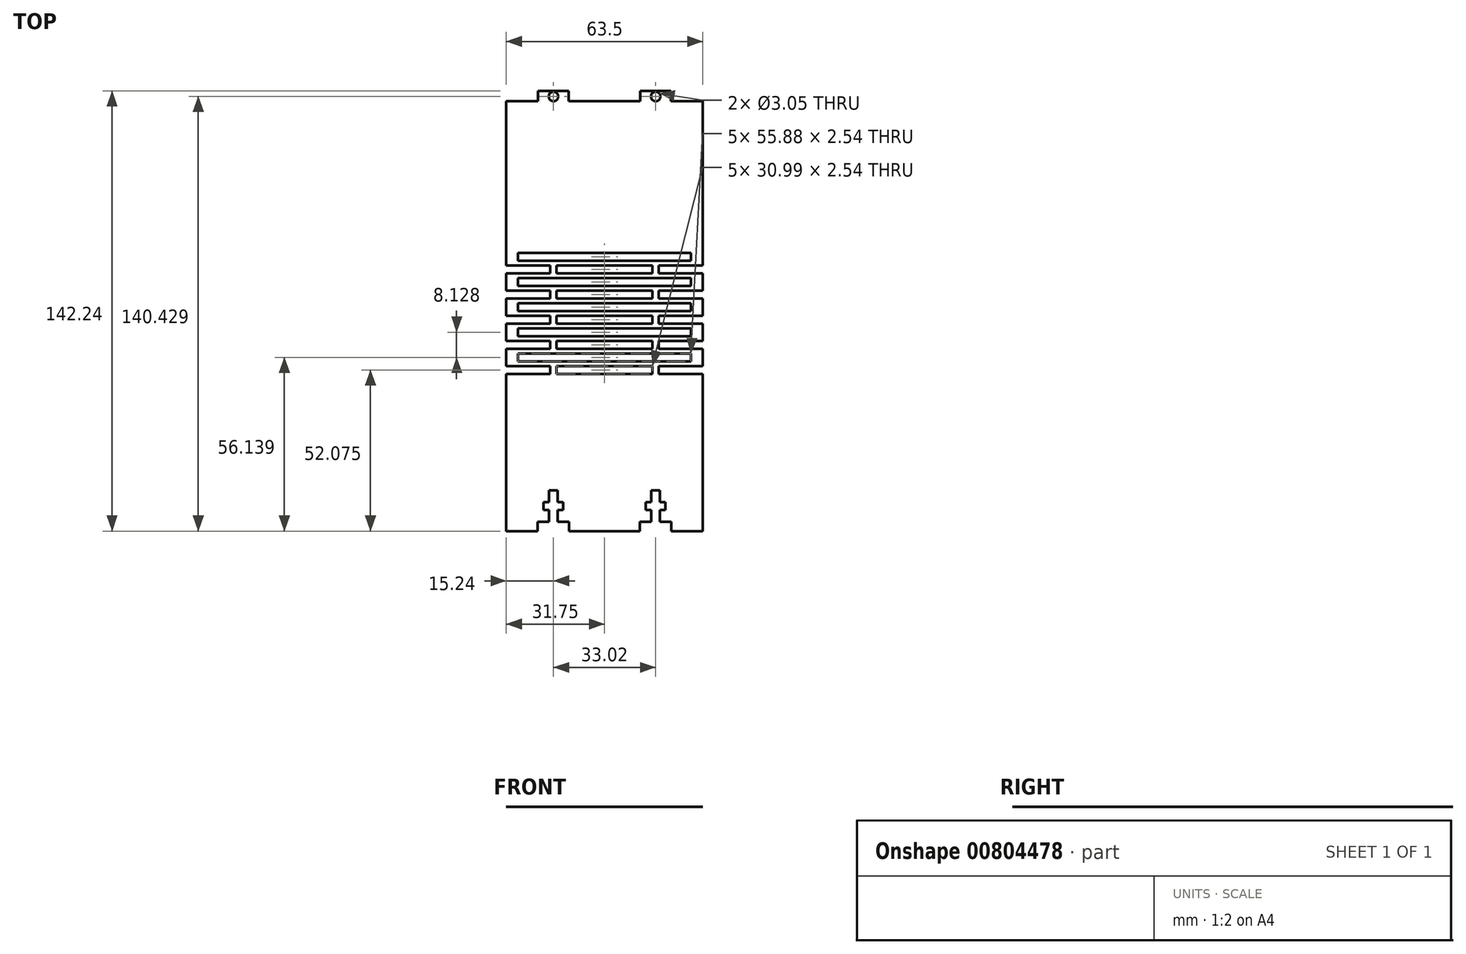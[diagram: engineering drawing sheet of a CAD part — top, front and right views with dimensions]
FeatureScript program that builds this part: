
annotation { "Feature Type Name" : "Feature", "Feature Type Description" : "" }
export const myFeature = defineFeature(function(context is Context, id is Id, definition is map)
    precondition{}
    {
        {
            var Q0;
            Q0=qCreatedBy(makeId("Top.planeOp"),FACE);
            var sketch = newSketch(context, id + "F0", { "sketchPlane" : qUnion([Q0])});
            skLineSegment(sketch, "E0.bottom", {"start": v(31.75, -64.45) * mm, "end": v(-31.75, -64.45) * mm});
            skLineSegment(sketch, "E1", {"start": v(-21.59, -64.45) * mm, "end": v(-21.59, -61.4) * mm});
            skLineSegment(sketch, "E2", {"start": v(-21.59, -61.4) * mm, "end": v(-17.9, -61.4) * mm});
            skLineSegment(sketch, "E3", {"start": v(-17.9, -61.4) * mm, "end": v(-17.9, -57.59) * mm});
            skLineSegment(sketch, "E4", {"start": v(-17.9, -57.59) * mm, "end": v(-19.69, -57.59) * mm});
            skLineSegment(sketch, "E5", {"start": v(-19.69, -57.59) * mm, "end": v(-19.69, -55.05) * mm});
            skLineSegment(sketch, "E6", {"start": v(-19.69, -55.05) * mm, "end": v(-17.9, -55.05) * mm});
            skLineSegment(sketch, "E7", {"start": v(-17.9, -55.05) * mm, "end": v(-17.9, -51.24) * mm});
            skLineSegment(sketch, "E8", {"start": v(-17.9, -51.24) * mm, "end": v(-15.11, -51.24) * mm});
            skLineSegment(sketch, "E9", {"start": v(-15.11, -51.24) * mm, "end": v(-15.11, -55.05) * mm});
            skLineSegment(sketch, "E10", {"start": v(-15.11, -55.05) * mm, "end": v(-13.33, -55.05) * mm});
            skLineSegment(sketch, "E11", {"start": v(-13.33, -55.05) * mm, "end": v(-13.33, -57.59) * mm});
            skLineSegment(sketch, "E12", {"start": v(-13.33, -57.59) * mm, "end": v(-15.11, -57.59) * mm});
            skLineSegment(sketch, "E13", {"start": v(-15.11, -57.59) * mm, "end": v(-15.11, -61.4) * mm});
            skLineSegment(sketch, "E14", {"start": v(-15.11, -61.4) * mm, "end": v(-11.43, -61.4) * mm});
            skLineSegment(sketch, "E15", {"start": v(-11.43, -61.4) * mm, "end": v(-11.43, -64.45) * mm});
            skLineSegment(sketch, "E16", {"start": v(-17.9, -55.05) * mm, "end": v(-15.11, -55.05) * mm, "construction": true});
            skLineSegment(sketch, "E17", {"start": v(-17.9, -57.59) * mm, "end": v(-15.11, -57.59) * mm, "construction": true});
            skLineSegment(sketch, "E18", {"start": v(-17.9, -61.4) * mm, "end": v(-15.11, -61.4) * mm, "construction": true});
            skLineSegment(sketch, "E19", {"start": v(-17.9, -55.05) * mm, "end": v(-17.9, -57.59) * mm, "construction": true});
            skLineSegment(sketch, "E20", {"start": v(-15.11, -55.05) * mm, "end": v(-15.11, -57.59) * mm, "construction": true});
            skLineSegment(sketch, "E21", {"start": v(-21.46, 74.5) * mm, "end": v(-21.46, 77.8) * mm});
            skLineSegment(sketch, "E22", {"start": v(-21.46, 77.8) * mm, "end": v(-11.56, 77.8) * mm});
            skLineSegment(sketch, "E23", {"start": v(-11.56, 77.8) * mm, "end": v(-11.56, 74.5) * mm});
            skCircle(sketch, "E24", {"center": v(-16.5, 75.98) * mm, "radius": 1.52 * mm});
            skPoint(sketch, "E25", {"position": v(-16.5, 77.8) * mm});
            skLineSegment(sketch, "E26", {"start": v(-21.59, -64.45) * mm, "end": v(-11.43, -64.45) * mm, "construction": true});
            skPoint(sketch, "E27", {"position": v(-16.51, -64.45) * mm});
            skLineSegment(sketch, "E28", {"start": v(-16.51, -64.45) * mm, "end": v(-16.51, 77.8) * mm, "construction": true});
            skLineSegment(sketch, "E29.MirrorCS", {"start": v(17.9, -57.59) * mm, "end": v(15.11, -57.59) * mm, "construction": true});
            skLineSegment(sketch, "E30.MirrorCS", {"start": v(15.11, -55.05) * mm, "end": v(15.11, -57.59) * mm, "construction": true});
            skLineSegment(sketch, "E31.MirrorCS", {"start": v(17.9, -55.05) * mm, "end": v(15.11, -55.05) * mm, "construction": true});
            skLineSegment(sketch, "E32.MirrorCS", {"start": v(17.9, -55.05) * mm, "end": v(17.9, -57.59) * mm, "construction": true});
            skLineSegment(sketch, "E33.MirrorCS", {"start": v(17.9, -57.59) * mm, "end": v(19.69, -57.59) * mm});
            skLineSegment(sketch, "E34.MirrorCS", {"start": v(17.9, -61.4) * mm, "end": v(15.11, -61.4) * mm, "construction": true});
            skLineSegment(sketch, "E35.MirrorCS", {"start": v(15.11, -55.05) * mm, "end": v(13.33, -55.05) * mm});
            skLineSegment(sketch, "E36.MirrorCS", {"start": v(17.9, -51.24) * mm, "end": v(15.11, -51.24) * mm});
            skLineSegment(sketch, "E37.MirrorCS", {"start": v(11.43, -61.4) * mm, "end": v(11.43, -64.45) * mm});
            skLineSegment(sketch, "E38.MirrorCS", {"start": v(19.69, -55.05) * mm, "end": v(17.9, -55.05) * mm});
            skLineSegment(sketch, "E39.MirrorCS", {"start": v(19.69, -57.59) * mm, "end": v(19.69, -55.05) * mm});
            skLineSegment(sketch, "E40.MirrorCS", {"start": v(13.33, -55.05) * mm, "end": v(13.33, -57.59) * mm});
            skLineSegment(sketch, "E41.MirrorCS", {"start": v(13.33, -57.59) * mm, "end": v(15.11, -57.59) * mm});
            skLineSegment(sketch, "E42.MirrorCS", {"start": v(21.59, -64.45) * mm, "end": v(21.59, -61.4) * mm});
            skLineSegment(sketch, "E43.MirrorCS", {"start": v(17.9, -55.05) * mm, "end": v(17.9, -51.24) * mm});
            skLineSegment(sketch, "E44.MirrorCS", {"start": v(21.59, -64.45) * mm, "end": v(11.43, -64.45) * mm, "construction": true});
            skLineSegment(sketch, "E45.MirrorCS", {"start": v(15.11, -51.24) * mm, "end": v(15.11, -55.05) * mm});
            skLineSegment(sketch, "E46.MirrorCS", {"start": v(15.11, -57.59) * mm, "end": v(15.11, -61.4) * mm});
            skLineSegment(sketch, "E47.MirrorCS", {"start": v(17.9, -61.4) * mm, "end": v(17.9, -57.59) * mm});
            skLineSegment(sketch, "E48.MirrorCS", {"start": v(-31.75, -64.45) * mm, "end": v(31.75, -64.45) * mm});
            skLineSegment(sketch, "E49.MirrorCS", {"start": v(21.59, -61.4) * mm, "end": v(17.9, -61.4) * mm});
            skPoint(sketch, "E50.MirrorP", {"position": v(16.51, -64.45) * mm});
            skLineSegment(sketch, "E51.MirrorCS", {"start": v(16.51, -64.45) * mm, "end": v(16.51, 77.8) * mm, "construction": true});
            skLineSegment(sketch, "E52.MirrorCS", {"start": v(15.11, -61.4) * mm, "end": v(11.43, -61.4) * mm});
            skLineSegment(sketch, "E53.bottom", {"start": v(27.94, 22.93) * mm, "end": v(-27.94, 22.93) * mm});
            skLineSegment(sketch, "E53.top", {"start": v(27.94, 25.47) * mm, "end": v(-27.94, 25.47) * mm});
            skLineSegment(sketch, "E53.left", {"start": v(27.94, 22.93) * mm, "end": v(27.94, 25.47) * mm});
            skLineSegment(sketch, "E53.right", {"start": v(-27.94, 22.93) * mm, "end": v(-27.94, 25.47) * mm});
            skPoint(sketch, "E53.middle", {"position": v(0, 24.2) * mm});
            skLineSegment(sketch, "E54", {"start": v(0, 21.66) * mm, "end": v(0, 26.74) * mm, "construction": true});
            skLineSegment(sketch, "E55.left", {"start": v(-17.53, 21.4) * mm, "end": v(-17.53, 18.87) * mm});
            skLineSegment(sketch, "E55.right", {"start": v(-15.5, 21.4) * mm, "end": v(-15.5, 18.87) * mm});
            skLineSegment(sketch, "E56", {"start": v(-17.53, 20.14) * mm, "end": v(-15.5, 20.14) * mm, "construction": true});
            skLineSegment(sketch, "E57.MirrorCS", {"start": v(15.5, 21.4) * mm, "end": v(15.5, 18.87) * mm});
            skLineSegment(sketch, "E58.MirrorCS", {"start": v(17.53, 21.4) * mm, "end": v(17.53, 18.87) * mm});
            skLineSegment(sketch, "E59", {"start": v(-31.75, 21.4) * mm, "end": v(-17.53, 21.4) * mm});
            skLineSegment(sketch, "E60", {"start": v(-15.5, 21.4) * mm, "end": v(15.5, 21.4) * mm});
            skLineSegment(sketch, "E61", {"start": v(17.53, 21.4) * mm, "end": v(31.75, 21.4) * mm});
            skLineSegment(sketch, "E62", {"start": v(-31.75, -64.45) * mm, "end": v(-31.75, -13.65) * mm});
            skLineSegment(sketch, "E63", {"start": v(31.75, -13.65) * mm, "end": v(31.75, -64.45) * mm});
            skLineSegment(sketch, "E64.direction1", {"start": v(-31.75, 21.4) * mm, "end": v(-4.72, 21.4) * mm, "construction": true});
            skLineSegment(sketch, "E65", {"start": v(-31.75, 27) * mm, "end": v(31.75, 27) * mm});
            skLineSegment(sketch, "E66", {"start": v(-31.75, 74.5) * mm, "end": v(-31.75, 27) * mm});
            skLineSegment(sketch, "E67", {"start": v(31.75, 74.5) * mm, "end": v(31.75, 27) * mm});
            skLineSegment(sketch, "E68", {"start": v(-31.75, 27) * mm, "end": v(-31.75, 21.4) * mm});
            skLineSegment(sketch, "E69", {"start": v(31.75, 27) * mm, "end": v(31.75, 21.4) * mm});
            skLineSegment(sketch, "E70", {"start": v(-27.94, 24.2) * mm, "end": v(-31.75, 24.2) * mm, "construction": true});
            skLineSegment(sketch, "E71", {"start": v(27.94, 24.2) * mm, "end": v(31.75, 24.2) * mm, "construction": true});
            skLineSegment(sketch, "E72.0.1.0", {"start": v(17.53, 13.28) * mm, "end": v(31.75, 13.28) * mm});
            skLineSegment(sketch, "E72.0.1.1", {"start": v(-17.53, 12) * mm, "end": v(-15.5, 12) * mm, "construction": true});
            skLineSegment(sketch, "E72.0.1.2", {"start": v(0, 13.53) * mm, "end": v(0, 18.61) * mm, "construction": true});
            skLineSegment(sketch, "E72.0.1.3", {"start": v(15.5, 13.28) * mm, "end": v(15.5, 10.74) * mm});
            skPoint(sketch, "E72.0.1.5", {"position": v(0, 16.07) * mm});
            skLineSegment(sketch, "E72.0.1.6", {"start": v(-15.5, 13.28) * mm, "end": v(15.5, 13.28) * mm});
            skLineSegment(sketch, "E72.0.1.7", {"start": v(27.94, 17.34) * mm, "end": v(-27.94, 17.34) * mm});
            skLineSegment(sketch, "E72.0.1.8", {"start": v(-31.75, 18.87) * mm, "end": v(-31.75, 13.28) * mm});
            skLineSegment(sketch, "E72.0.1.9", {"start": v(17.53, 13.28) * mm, "end": v(17.53, 10.74) * mm});
            skLineSegment(sketch, "E72.0.1.10", {"start": v(-27.94, 16.07) * mm, "end": v(-31.75, 16.07) * mm, "construction": true});
            skLineSegment(sketch, "E72.0.1.11", {"start": v(27.94, 14.8) * mm, "end": v(-27.94, 14.8) * mm});
            skLineSegment(sketch, "E72.0.1.12", {"start": v(-31.75, 13.28) * mm, "end": v(-4.72, 13.28) * mm, "construction": true});
            skLineSegment(sketch, "E72.0.1.13", {"start": v(31.75, 18.87) * mm, "end": v(31.75, 13.28) * mm});
            skLineSegment(sketch, "E72.0.1.14", {"start": v(27.94, 16.07) * mm, "end": v(31.75, 16.07) * mm, "construction": true});
            skLineSegment(sketch, "E72.0.1.15", {"start": v(27.94, 14.8) * mm, "end": v(27.94, 17.34) * mm});
            skLineSegment(sketch, "E72.0.1.16", {"start": v(-31.75, 13.28) * mm, "end": v(-17.53, 13.28) * mm});
            skLineSegment(sketch, "E72.0.1.17", {"start": v(-17.53, 13.28) * mm, "end": v(-17.53, 10.74) * mm});
            skLineSegment(sketch, "E72.0.1.18", {"start": v(-27.94, 14.8) * mm, "end": v(-27.94, 17.34) * mm});
            skLineSegment(sketch, "E72.0.1.19", {"start": v(-15.5, 13.28) * mm, "end": v(-15.5, 10.74) * mm});
            skLineSegment(sketch, "E72.0.2.0", {"start": v(17.53, 5.15) * mm, "end": v(31.75, 5.15) * mm});
            skLineSegment(sketch, "E72.0.2.1", {"start": v(-17.53, 3.88) * mm, "end": v(-15.5, 3.88) * mm, "construction": true});
            skLineSegment(sketch, "E72.0.2.2", {"start": v(0, 5.4) * mm, "end": v(0, 10.48) * mm, "construction": true});
            skLineSegment(sketch, "E72.0.2.3", {"start": v(15.5, 5.15) * mm, "end": v(15.5, 2.61) * mm});
            skPoint(sketch, "E72.0.2.5", {"position": v(0, 7.94) * mm});
            skLineSegment(sketch, "E72.0.2.6", {"start": v(-15.5, 5.15) * mm, "end": v(15.5, 5.15) * mm});
            skLineSegment(sketch, "E72.0.2.7", {"start": v(27.94, 9.21) * mm, "end": v(-27.94, 9.21) * mm});
            skLineSegment(sketch, "E72.0.2.8", {"start": v(-31.75, 10.74) * mm, "end": v(-31.75, 5.15) * mm});
            skLineSegment(sketch, "E72.0.2.9", {"start": v(17.53, 5.15) * mm, "end": v(17.53, 2.61) * mm});
            skLineSegment(sketch, "E72.0.2.10", {"start": v(-27.94, 7.94) * mm, "end": v(-31.75, 7.94) * mm, "construction": true});
            skLineSegment(sketch, "E72.0.2.11", {"start": v(27.94, 6.67) * mm, "end": v(-27.94, 6.67) * mm});
            skLineSegment(sketch, "E72.0.2.12", {"start": v(-31.75, 5.15) * mm, "end": v(-4.72, 5.15) * mm, "construction": true});
            skLineSegment(sketch, "E72.0.2.13", {"start": v(31.75, 10.74) * mm, "end": v(31.75, 5.15) * mm});
            skLineSegment(sketch, "E72.0.2.14", {"start": v(27.94, 7.94) * mm, "end": v(31.75, 7.94) * mm, "construction": true});
            skLineSegment(sketch, "E72.0.2.15", {"start": v(27.94, 6.67) * mm, "end": v(27.94, 9.21) * mm});
            skLineSegment(sketch, "E72.0.2.16", {"start": v(-31.75, 5.15) * mm, "end": v(-17.53, 5.15) * mm});
            skLineSegment(sketch, "E72.0.2.17", {"start": v(-17.53, 5.15) * mm, "end": v(-17.53, 2.61) * mm});
            skLineSegment(sketch, "E72.0.2.18", {"start": v(-27.94, 6.67) * mm, "end": v(-27.94, 9.21) * mm});
            skLineSegment(sketch, "E72.0.2.19", {"start": v(-15.5, 5.15) * mm, "end": v(-15.5, 2.61) * mm});
            skLineSegment(sketch, "E72.0.3.0", {"start": v(17.53, -2.98) * mm, "end": v(31.75, -2.98) * mm});
            skLineSegment(sketch, "E72.0.3.1", {"start": v(-17.53, -4.25) * mm, "end": v(-15.5, -4.25) * mm, "construction": true});
            skLineSegment(sketch, "E72.0.3.2", {"start": v(0, -2.72) * mm, "end": v(0, 2.36) * mm, "construction": true});
            skLineSegment(sketch, "E72.0.3.3", {"start": v(15.5, -2.98) * mm, "end": v(15.5, -5.52) * mm});
            skPoint(sketch, "E72.0.3.5", {"position": v(0, -0.18) * mm});
            skLineSegment(sketch, "E72.0.3.6", {"start": v(-15.5, -2.98) * mm, "end": v(15.5, -2.98) * mm});
            skLineSegment(sketch, "E72.0.3.7", {"start": v(27.94, 1.09) * mm, "end": v(-27.94, 1.09) * mm});
            skLineSegment(sketch, "E72.0.3.8", {"start": v(-31.75, 2.61) * mm, "end": v(-31.75, -2.98) * mm});
            skLineSegment(sketch, "E72.0.3.9", {"start": v(17.53, -2.98) * mm, "end": v(17.53, -5.52) * mm});
            skLineSegment(sketch, "E72.0.3.10", {"start": v(-27.94, -0.18) * mm, "end": v(-31.75, -0.18) * mm, "construction": true});
            skLineSegment(sketch, "E72.0.3.11", {"start": v(27.94, -1.45) * mm, "end": v(-27.94, -1.45) * mm});
            skLineSegment(sketch, "E72.0.3.12", {"start": v(-31.75, -2.98) * mm, "end": v(-4.72, -2.98) * mm, "construction": true});
            skLineSegment(sketch, "E72.0.3.13", {"start": v(31.75, 2.61) * mm, "end": v(31.75, -2.98) * mm});
            skLineSegment(sketch, "E72.0.3.14", {"start": v(27.94, -0.18) * mm, "end": v(31.75, -0.18) * mm, "construction": true});
            skLineSegment(sketch, "E72.0.3.15", {"start": v(27.94, -1.45) * mm, "end": v(27.94, 1.09) * mm});
            skLineSegment(sketch, "E72.0.3.16", {"start": v(-31.75, -2.98) * mm, "end": v(-17.53, -2.98) * mm});
            skLineSegment(sketch, "E72.0.3.17", {"start": v(-17.53, -2.98) * mm, "end": v(-17.53, -5.52) * mm});
            skLineSegment(sketch, "E72.0.3.18", {"start": v(-27.94, -1.45) * mm, "end": v(-27.94, 1.09) * mm});
            skLineSegment(sketch, "E72.0.3.19", {"start": v(-15.5, -2.98) * mm, "end": v(-15.5, -5.52) * mm});
            skLineSegment(sketch, "E72.0.4.0", {"start": v(17.53, -11.1) * mm, "end": v(31.75, -11.1) * mm});
            skLineSegment(sketch, "E72.0.4.1", {"start": v(-17.53, -12.38) * mm, "end": v(-15.5, -12.38) * mm, "construction": true});
            skLineSegment(sketch, "E72.0.4.2", {"start": v(0, -10.85) * mm, "end": v(0, -5.77) * mm, "construction": true});
            skLineSegment(sketch, "E72.0.4.3", {"start": v(15.5, -11.1) * mm, "end": v(15.5, -13.65) * mm});
            skPoint(sketch, "E72.0.4.5", {"position": v(0, -8.31) * mm});
            skLineSegment(sketch, "E72.0.4.6", {"start": v(-15.5, -11.1) * mm, "end": v(15.5, -11.1) * mm});
            skLineSegment(sketch, "E72.0.4.7", {"start": v(27.94, -7.04) * mm, "end": v(-27.94, -7.04) * mm});
            skLineSegment(sketch, "E72.0.4.8", {"start": v(-31.75, -5.52) * mm, "end": v(-31.75, -11.1) * mm});
            skLineSegment(sketch, "E72.0.4.9", {"start": v(17.53, -11.1) * mm, "end": v(17.53, -13.65) * mm});
            skLineSegment(sketch, "E72.0.4.10", {"start": v(-27.94, -8.31) * mm, "end": v(-31.75, -8.31) * mm, "construction": true});
            skLineSegment(sketch, "E72.0.4.11", {"start": v(27.94, -9.58) * mm, "end": v(-27.94, -9.58) * mm});
            skLineSegment(sketch, "E72.0.4.12", {"start": v(-31.75, -11.1) * mm, "end": v(-4.72, -11.1) * mm, "construction": true});
            skLineSegment(sketch, "E72.0.4.13", {"start": v(31.75, -5.52) * mm, "end": v(31.75, -11.1) * mm});
            skLineSegment(sketch, "E72.0.4.14", {"start": v(27.94, -8.31) * mm, "end": v(31.75, -8.31) * mm, "construction": true});
            skLineSegment(sketch, "E72.0.4.15", {"start": v(27.94, -9.58) * mm, "end": v(27.94, -7.04) * mm});
            skLineSegment(sketch, "E72.0.4.16", {"start": v(-31.75, -11.1) * mm, "end": v(-17.53, -11.1) * mm});
            skLineSegment(sketch, "E72.0.4.17", {"start": v(-17.53, -11.1) * mm, "end": v(-17.53, -13.65) * mm});
            skLineSegment(sketch, "E72.0.4.18", {"start": v(-27.94, -9.58) * mm, "end": v(-27.94, -7.04) * mm});
            skLineSegment(sketch, "E72.0.4.19", {"start": v(-15.5, -11.1) * mm, "end": v(-15.5, -13.65) * mm});
            skLineSegment(sketch, "E72.direction1", {"start": v(-31.75, 21.4) * mm, "end": v(-6.35, 21.4) * mm, "construction": true});
            skLineSegment(sketch, "E72.direction2", {"start": v(-31.75, 21.4) * mm, "end": v(-31.75, 13.28) * mm, "construction": true});
            skLineSegment(sketch, "E73", {"start": v(-17.53, -13.65) * mm, "end": v(-31.75, -13.65) * mm});
            skLineSegment(sketch, "E74", {"start": v(31.75, -13.65) * mm, "end": v(17.53, -13.65) * mm});
            skLineSegment(sketch, "E75", {"start": v(-15.5, -13.65) * mm, "end": v(15.5, -13.65) * mm});
            skPoint(sketch, "E76", {"position": v(-16.51, 20.14) * mm});
            skLineSegment(sketch, "E77", {"start": v(-31.75, 74.5) * mm, "end": v(-21.46, 74.5) * mm});
            skLineSegment(sketch, "E78.MirrorCS", {"start": v(21.46, 77.8) * mm, "end": v(11.56, 77.8) * mm});
            skCircle(sketch, "E79.MirrorC", {"center": v(16.5, 75.98) * mm, "radius": 1.52 * mm});
            skLineSegment(sketch, "E80.MirrorCS", {"start": v(31.75, 74.5) * mm, "end": v(21.46, 74.5) * mm});
            skLineSegment(sketch, "E81.MirrorCS", {"start": v(11.56, 77.8) * mm, "end": v(11.56, 74.5) * mm});
            skPoint(sketch, "E82.MirrorP", {"position": v(16.5, 77.8) * mm});
            skLineSegment(sketch, "E83.MirrorCS", {"start": v(21.46, 74.5) * mm, "end": v(21.46, 77.8) * mm});
            skLineSegment(sketch, "E84", {"start": v(-11.56, 74.5) * mm, "end": v(11.56, 74.5) * mm});
            skLineSegment(sketch, "E85", {"start": v(-31.75, 18.87) * mm, "end": v(-17.53, 18.87) * mm});
            skLineSegment(sketch, "E86", {"start": v(-15.5, 18.87) * mm, "end": v(15.5, 18.87) * mm});
            skLineSegment(sketch, "E87", {"start": v(17.53, 18.87) * mm, "end": v(31.75, 18.87) * mm});
            skLineSegment(sketch, "E88", {"start": v(-31.75, 10.74) * mm, "end": v(-17.53, 10.74) * mm});
            skLineSegment(sketch, "E89", {"start": v(-15.5, 10.74) * mm, "end": v(15.5, 10.74) * mm});
            skLineSegment(sketch, "E90", {"start": v(17.53, 10.74) * mm, "end": v(31.75, 10.74) * mm});
            skLineSegment(sketch, "E91", {"start": v(-31.75, 2.61) * mm, "end": v(-17.53, 2.61) * mm});
            skLineSegment(sketch, "E92", {"start": v(-15.5, 2.61) * mm, "end": v(15.5, 2.61) * mm});
            skLineSegment(sketch, "E93", {"start": v(17.53, 2.61) * mm, "end": v(31.75, 2.61) * mm});
            skLineSegment(sketch, "E94", {"start": v(-31.75, -5.52) * mm, "end": v(-17.53, -5.52) * mm});
            skLineSegment(sketch, "E95", {"start": v(-15.5, -5.52) * mm, "end": v(15.5, -5.52) * mm});
            skLineSegment(sketch, "E96", {"start": v(17.53, -5.52) * mm, "end": v(31.75, -5.52) * mm});
            skSolve(sketch);
        }
        {
            var Q0;
            {var subQ13=sQuery(id+"F0.wireOp",EDGE,"E1");Q0=makeQuery(id+"F0.imprint","IMPRINT",FACE,{"disambiguationData":[TD([[makeQuery(id+"F0.imprint","IMPRINT",EDGE,{"derivedFrom":subQ13}),1.0]])]});}
            var Q1;
            {var subQ5=sQuery(id+"F0.wireOp",EDGE,"E21");Q1=makeQuery(id+"F0.imprint","IMPRINT",FACE,{"disambiguationData":[TD([[makeQuery(id+"F0.imprint","IMPRINT",EDGE,{"derivedFrom":subQ5}),-1.0]])]});}
            var Q2;
            {var subQ5=sQuery(id+"F0.wireOp",EDGE,"E306.MirrorCS");Q2=makeQuery(id+"F0.imprint","IMPRINT",FACE,{"disambiguationData":[TD([[makeQuery(id+"F0.imprint","IMPRINT",EDGE,{"derivedFrom":subQ5}),1.0]])]});}
            var Q3;
            Q3=makeQuery(id+"F0.imprint","IMPRINT",FACE,{"disambiguationData":[TD([[makeQuery(id+"F0.imprint","IMPRINT",EDGE,{"derivedFrom":sQuery(id+"F0.wireOp",EDGE,"E65")}),1.0]])]});
            var Q4;
            Q4=makeQuery(id+"F0.imprint","IMPRINT",FACE,{"disambiguationData":[TD([[makeQuery(id+"F0.imprint","IMPRINT",EDGE,{"derivedFrom":sQuery(id+"F0.wireOp",EDGE,"E53.bottom")}),1.0]])]});
            var Q5;
            Q5=makeQuery(id+"F0.imprint","IMPRINT",FACE,{"disambiguationData":[TD([[makeQuery(id+"F0.imprint","IMPRINT",EDGE,{"derivedFrom":sQuery(id+"F0.wireOp",EDGE,"E72.0.1.0")}),1.0]])]});
            var Q6;
            Q6=makeQuery(id+"F0.imprint","IMPRINT",FACE,{"disambiguationData":[TD([[makeQuery(id+"F0.imprint","IMPRINT",EDGE,{"derivedFrom":sQuery(id+"F0.wireOp",EDGE,"E72.0.2.0")}),1.0]])]});
            var Q7;
            Q7=makeQuery(id+"F0.imprint","IMPRINT",FACE,{"disambiguationData":[TD([[makeQuery(id+"F0.imprint","IMPRINT",EDGE,{"derivedFrom":sQuery(id+"F0.wireOp",EDGE,"E72.0.3.0")}),1.0]])]});
            extrude(context, id + "F1", {"entities" : qUnion([Q0, Q1, Q2, Q3, Q4, Q5, Q6, Q7]), "depth" : 1 / 203.2 * mm, "offsetDistance" : 25.4 * mm});
        }
    });
